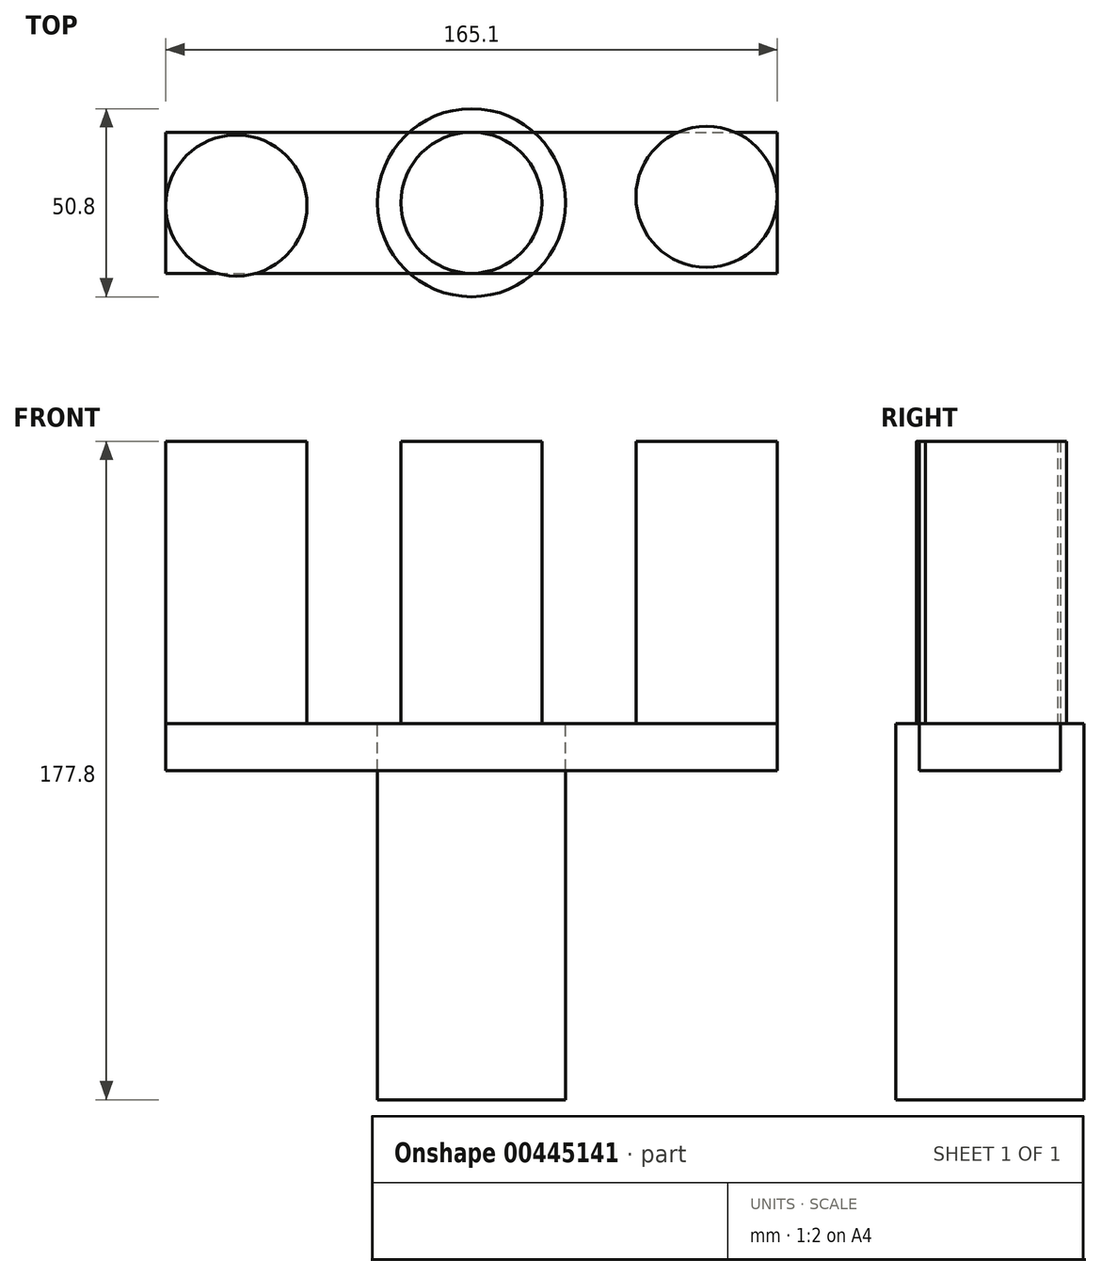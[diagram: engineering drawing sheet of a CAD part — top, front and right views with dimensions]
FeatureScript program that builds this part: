
annotation { "Feature Type Name" : "Feature", "Feature Type Description" : "" }
export const myFeature = defineFeature(function(context is Context, id is Id, definition is map)
    precondition{}
    {
        {
            var Q0;
            Q0=qCreatedBy(makeId("Top.planeOp"),FACE);
            var sketch = newSketch(context, id + "F0", { "sketchPlane" : qUnion([Q0])});
            skCircle(sketch, "E0", {"center": v(0, 0) * mm, "radius": 19.05 * mm});
            skLineSegment(sketch, "E1", {"start": v(19.05, 0) * mm, "end": v(44.45, 0) * mm});
            skLineSegment(sketch, "E2", {"start": v(-19.05, 0) * mm, "end": v(-44.45, 0) * mm});
            skCircle(sketch, "E3", {"center": v(-63.48, -0.76) * mm, "radius": 19.05 * mm});
            skPoint(sketch, "E3.second.point", {"position": v(-82.52, 0) * mm});
            skPoint(sketch, "E3.third.point", {"position": v(-81.3, -7.49) * mm});
            skCircle(sketch, "E4", {"center": v(63.43, 1.61) * mm, "radius": 19.05 * mm});
            skPoint(sketch, "E4.second.point", {"position": v(82.41, 0) * mm});
            skPoint(sketch, "E4.third.point", {"position": v(55.7, 19.02) * mm});
            skSolve(sketch);
        }
        {
            var Q0;
            Q0=qCreatedBy(makeId("Top.planeOp"),FACE);
            var sketch = newSketch(context, id + "F1", { "sketchPlane" : qUnion([Q0])});
            skLineSegment(sketch, "E5.bottom", {"start": v(-82.55, 19.05) * mm, "end": v(82.55, 19.05) * mm});
            skLineSegment(sketch, "E5.top", {"start": v(-82.55, -19.05) * mm, "end": v(82.55, -19.05) * mm});
            skLineSegment(sketch, "E5.left", {"start": v(-82.55, 19.05) * mm, "end": v(-82.55, -19.05) * mm});
            skLineSegment(sketch, "E5.right", {"start": v(82.55, 19.05) * mm, "end": v(82.55, -19.05) * mm});
            skPoint(sketch, "E5.middle", {"position": v(0, 0) * mm});
            skSolve(sketch);
        }
        {
            var Q0;
            Q0=qCreatedBy(makeId("Top.planeOp"),FACE);
            var sketch = newSketch(context, id + "F2", { "sketchPlane" : qUnion([Q0])});
            skCircle(sketch, "E6", {"center": v(0, 0) * mm, "radius": 25.4 * mm});
            skSolve(sketch);
        }
        {
            var Q0;
            Q0 = qSketchRegion(id + "F0", true);
            extrude(context, id + "F3", {"entities" : qUnion([Q0]), "depth" : 76.2 * mm});
        }
        {
            var Q0;
            Q0 = qSketchRegion(id + "F1", true);
            extrude(context, id + "F4", {"entities" : qUnion([Q0]), "oppositeDirection" : true, "depth" : 12.7 * mm});
        }
        {
            var Q0;
            Q0 = qSketchRegion(id + "F2", true);
            extrude(context, id + "F5", {"entities" : qUnion([Q0]), "oppositeDirection" : true, "depth" : 101.6 * mm});
        }
    });
